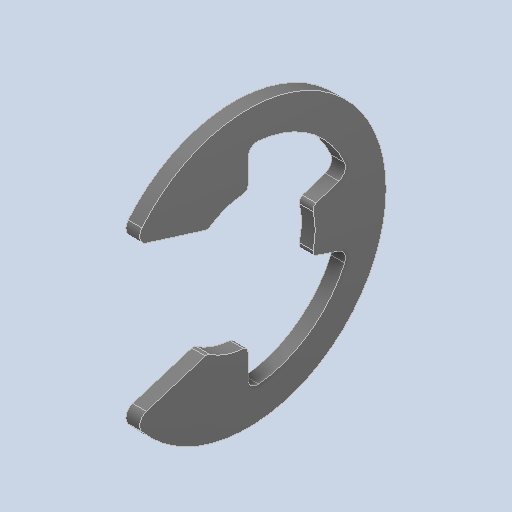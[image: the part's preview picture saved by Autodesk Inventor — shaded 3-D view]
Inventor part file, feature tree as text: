
AUTODESK INVENTOR PART (.ipt)
format: ipt  version: 2024.2 (Build 282272000, 272)  size: 116,736 bytes
history: native  units: in
note: dims shown in document units (in); Inventor stores cm internally (conversion verified against a paired STEP export)
features: fillet x1
ambient origin geometry x8: Origin, YZ Plane, XZ Plane, XY Plane, X Axis, Y Axis, Z Axis, Center Point
bodies: Solid1 (feature_tree)
feature tree (1):
  fillet  "Fillet2"  [1 undecoded]
note: 1 required parameter value undecoded (feature->parameter linkage not recoverable at this tier; creation-order binding heuristic only, values carry confidence <= 0.55)
